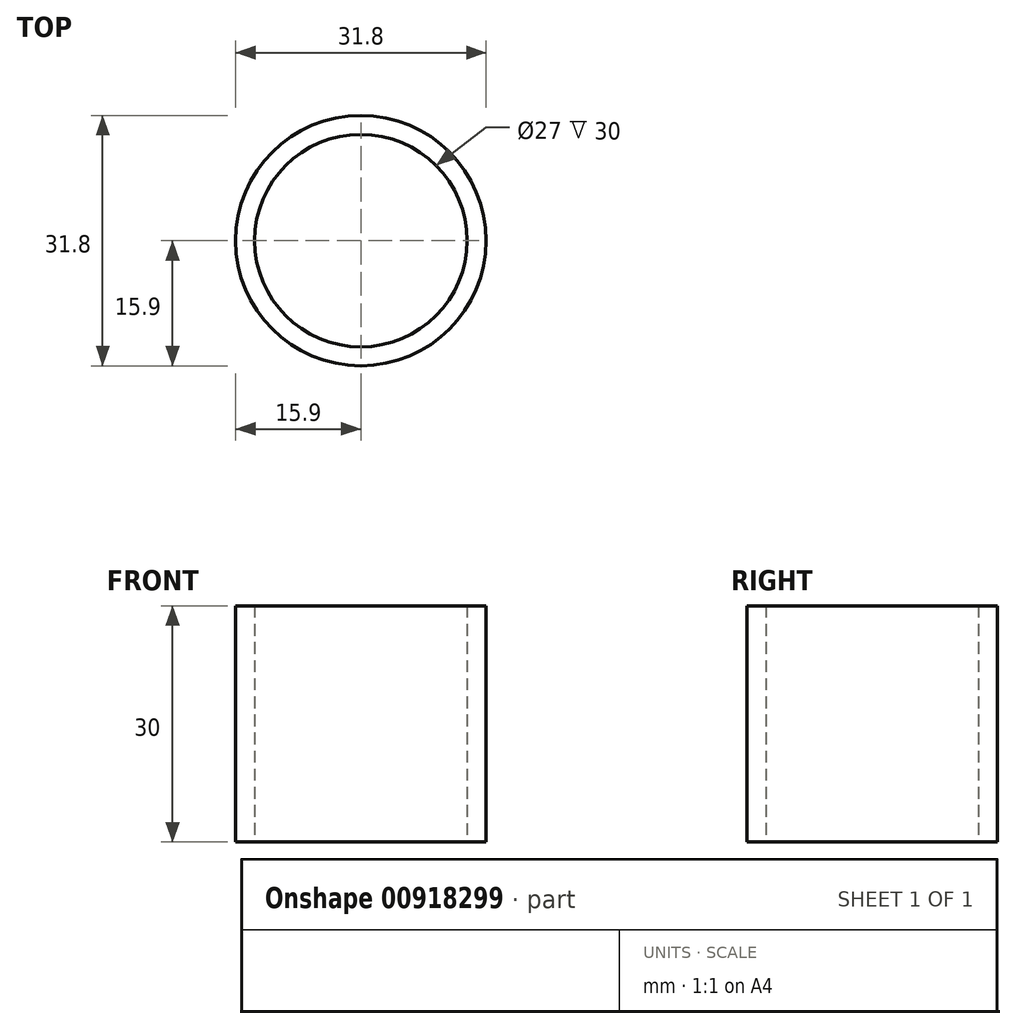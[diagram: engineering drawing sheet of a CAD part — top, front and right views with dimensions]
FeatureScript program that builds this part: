
annotation { "Feature Type Name" : "Feature", "Feature Type Description" : "" }
export const myFeature = defineFeature(function(context is Context, id is Id, definition is map)
    precondition{}
    {
        {
            var Q0;
            Q0=qCreatedBy(makeId("Top.planeOp"),FACE);
            var sketch = newSketch(context, id + "F0", { "sketchPlane" : qUnion([Q0])});
            skCircle(sketch, "E0", {"center": v(0, 0) * mm, "radius": 13.5 * mm});
            skCircle(sketch, "E1", {"center": v(0, 0) * mm, "radius": 15.9 * mm});
            skSolve(sketch);
        }
        {
            var Q0;
            Q0=makeQuery(id+"F0.imprint","IMPRINT",FACE,{"disambiguationData":[TD([[makeQuery(id+"F0.imprint","IMPRINT",EDGE,{"derivedFrom":sQuery(id+"F0.wireOp",EDGE,"E0")}),-1.0]])]});
            extrude(context, id + "F1", {"entities" : qUnion([Q0]), "depth" : 30 * mm, "offsetDistance" : 25 * mm});
        }
    });
